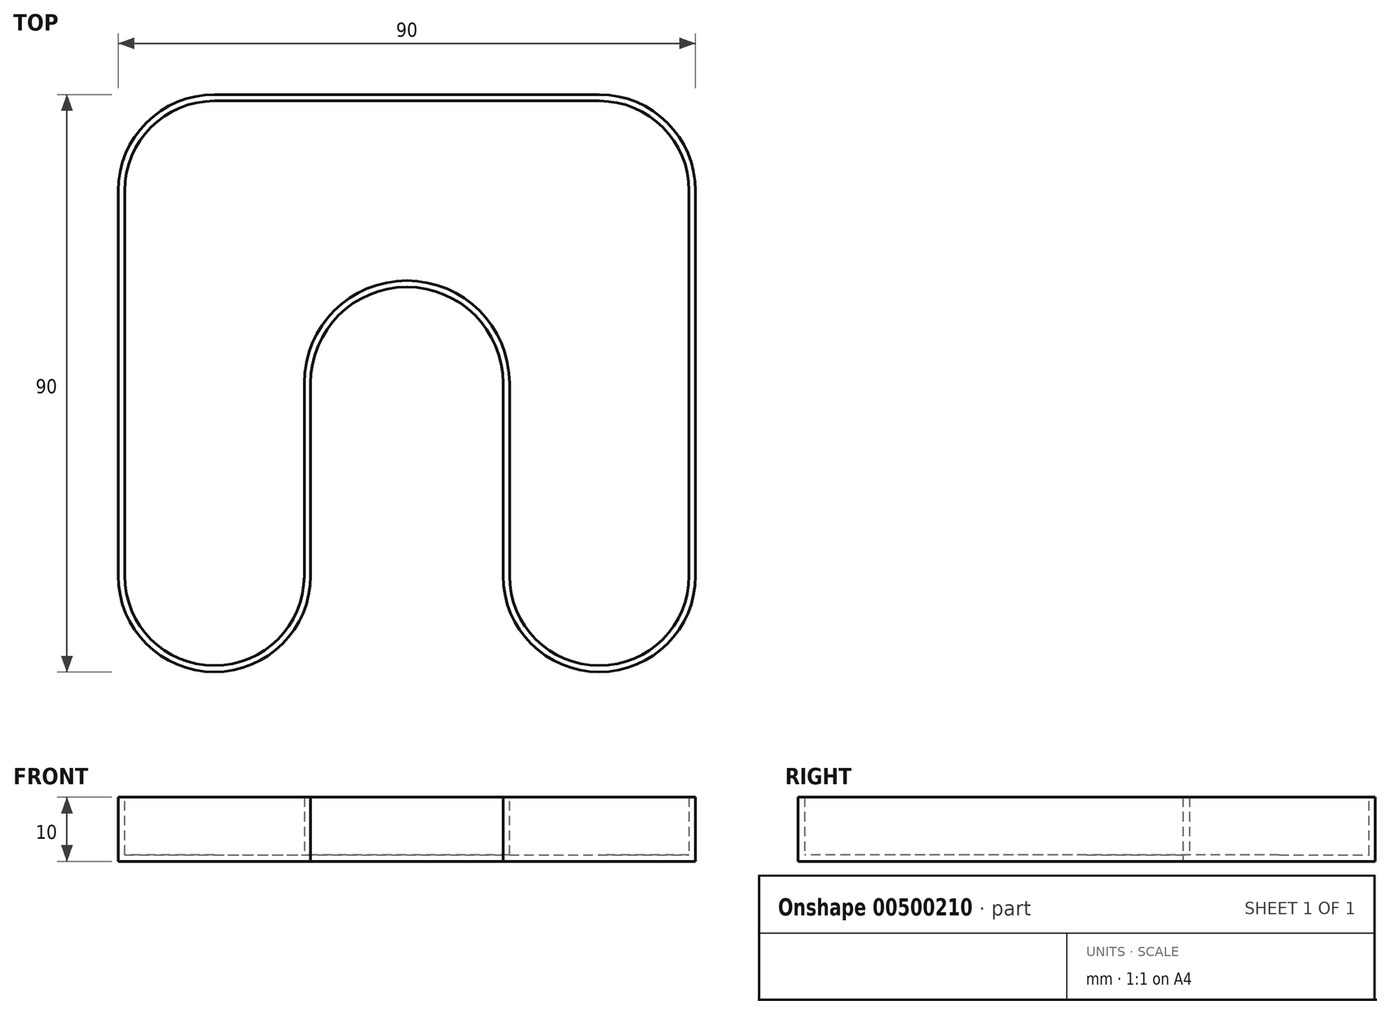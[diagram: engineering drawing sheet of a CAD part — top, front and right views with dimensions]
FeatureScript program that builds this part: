
annotation { "Feature Type Name" : "Feature", "Feature Type Description" : "" }
export const myFeature = defineFeature(function(context is Context, id is Id, definition is map)
    precondition{}
    {
        {
            var Q0;
            Q0=qCreatedBy(makeId("Top.planeOp"),FACE);
            var sketch = newSketch(context, id + "F0", { "sketchPlane" : qUnion([Q0])});
            skLineSegment(sketch, "E0", {"start": v(-90, 15) * mm, "end": v(-90, 75) * mm});
            skLineSegment(sketch, "E1", {"start": v(-75, 90) * mm, "end": v(-15, 90) * mm});
            skLineSegment(sketch, "E2", {"start": v(0, 75) * mm, "end": v(0, 15) * mm});
            skLineSegment(sketch, "E3", {"start": v(-15, 0) * mm, "end": v(-15, 0) * mm});
            skLineSegment(sketch, "E4", {"start": v(-30, 15) * mm, "end": v(-30, 45) * mm});
            skLineSegment(sketch, "E5", {"start": v(-45, 60) * mm, "end": v(-45, 60) * mm});
            skLineSegment(sketch, "E6", {"start": v(-60, 45) * mm, "end": v(-60, 15) * mm});
            skLineSegment(sketch, "E7", {"start": v(-75, 0) * mm, "end": v(-75, 0) * mm});
            skPoint(sketch, "E8.visualSharp", {"position": v(-90, 90) * mm});
            skArc(sketch, "E8.filletArc", {"start": v(-75, 90) * mm, "mid": v(-85.6, 85.6) * mm, "end": v(-90, 75) * mm});
            skPoint(sketch, "E9.visualSharp", {"position": v(0, 90) * mm});
            skArc(sketch, "E9.filletArc", {"start": v(0, 75) * mm, "mid": v(-4.4, 85.6) * mm, "end": v(-15, 90) * mm});
            skPoint(sketch, "E10.visualSharp", {"position": v(0, 0) * mm});
            skArc(sketch, "E10.filletArc", {"start": v(-15, 0) * mm, "mid": v(-4.4, 4.4) * mm, "end": v(0, 15) * mm});
            skPoint(sketch, "E11.visualSharp", {"position": v(-30, 0) * mm});
            skArc(sketch, "E11.filletArc", {"start": v(-30, 15) * mm, "mid": v(-25.6, 4.4) * mm, "end": v(-15, 0) * mm});
            skPoint(sketch, "E12.visualSharp", {"position": v(-30, 60) * mm});
            skArc(sketch, "E12.filletArc", {"start": v(-30, 45) * mm, "mid": v(-34.4, 55.6) * mm, "end": v(-45, 60) * mm});
            skPoint(sketch, "E13.visualSharp", {"position": v(-60, 60) * mm});
            skArc(sketch, "E13.filletArc", {"start": v(-45, 60) * mm, "mid": v(-55.6, 55.6) * mm, "end": v(-60, 45) * mm});
            skPoint(sketch, "E14.visualSharp", {"position": v(-60, 0) * mm});
            skArc(sketch, "E14.filletArc", {"start": v(-75, 0) * mm, "mid": v(-64.4, 4.4) * mm, "end": v(-60, 15) * mm});
            skPoint(sketch, "E15.visualSharp", {"position": v(-90, 0) * mm});
            skArc(sketch, "E15.filletArc", {"start": v(-90, 15) * mm, "mid": v(-85.6, 4.4) * mm, "end": v(-75, 0) * mm});
            skSolve(sketch);
        }
        {
            var Q0;
            Q0 = qSketchRegion(id + "F0", true);
            var Q1;
            Q1=makeQuery(id+"F0.imprint","IMPRINT",FACE,{"disambiguationData":[TD([[makeQuery(id+"F0.imprint","IMPRINT",EDGE,{"derivedFrom":sQuery(id+"F0.wireOp",EDGE,"E0")}),-1.0]])]});
            extrude(context, id + "F1", {"entities" : qUnion([Q0, Q1]), "depth" : 10 * mm});
        }
        {
            var Q0;
            Q0=makeQuery(id+"F1.opExtrude","CAP_FACE",FACE,{"disambiguationData":[OSD([sQuery(id+"F0.wireOp",EDGE,"E0"),sQuery(id+"F0.wireOp",EDGE,"E1"),sQuery(id+"F0.wireOp",EDGE,"E2"),sQuery(id+"F0.wireOp",EDGE,"E4"),sQuery(id+"F0.wireOp",EDGE,"E6"),sQuery(id+"F0.wireOp",EDGE,"E8.filletArc"),sQuery(id+"F0.wireOp",EDGE,"E9.filletArc"),sQuery(id+"F0.wireOp",EDGE,"E10.filletArc"),sQuery(id+"F0.wireOp",EDGE,"E11.filletArc"),sQuery(id+"F0.wireOp",EDGE,"E12.filletArc"),sQuery(id+"F0.wireOp",EDGE,"E13.filletArc"),sQuery(id+"F0.wireOp",EDGE,"E14.filletArc"),sQuery(id+"F0.wireOp",EDGE,"E15.filletArc")])],"isStart":false});
            shell(context, id + "F2", {"entities" : qUnion([Q0]), "thickness" : 1 * mm});
        }
    });
